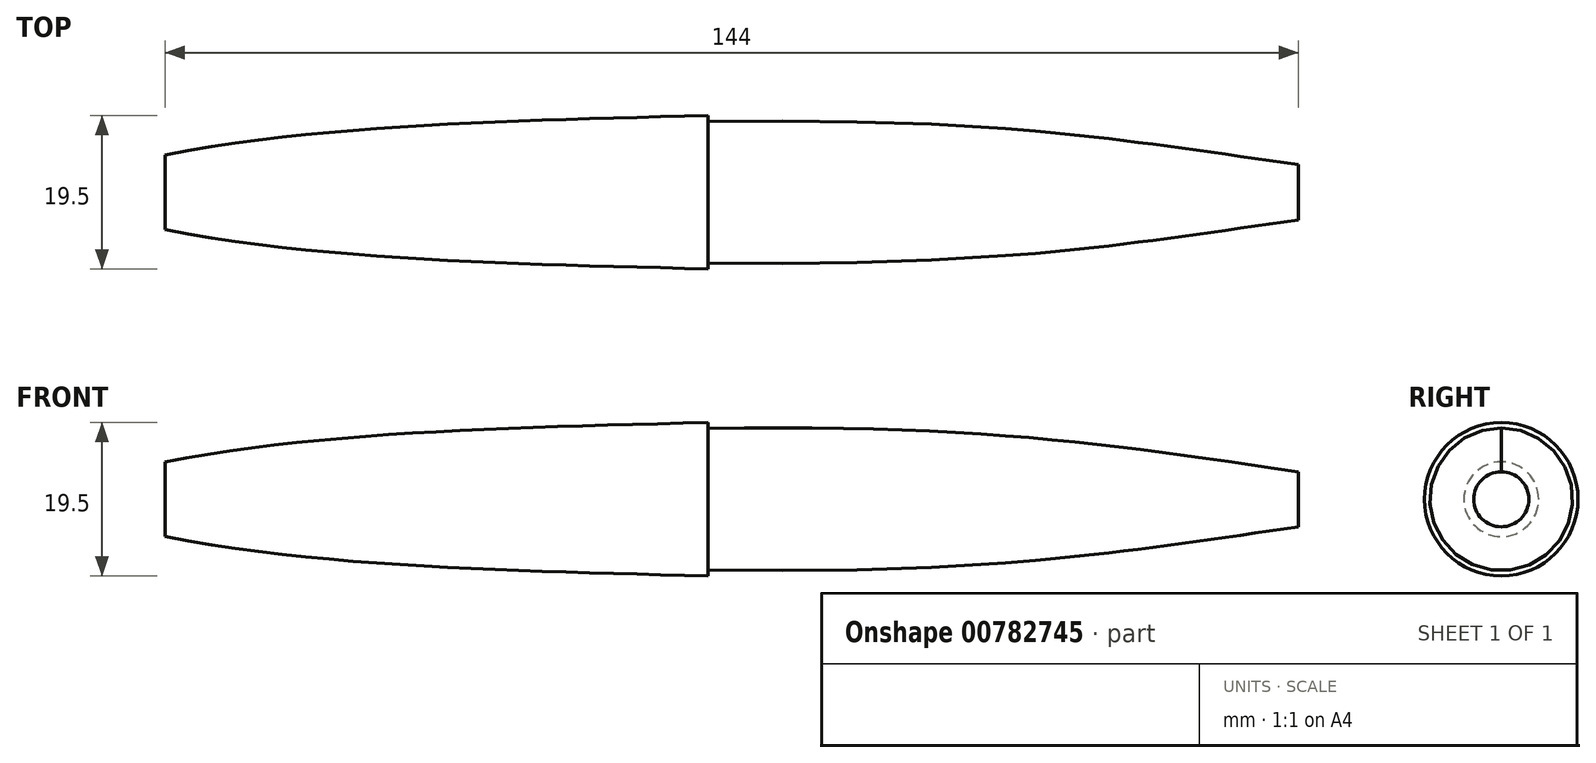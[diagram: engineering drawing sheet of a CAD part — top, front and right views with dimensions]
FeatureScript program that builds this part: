
annotation { "Feature Type Name" : "Feature", "Feature Type Description" : "" }
export const myFeature = defineFeature(function(context is Context, id is Id, definition is map)
    precondition{}
    {
        {
            var Q0;
            Q0=qCreatedBy(makeId("Front.planeOp"),FACE);
            var sketch = newSketch(context, id + "F0", { "sketchPlane" : qUnion([Q0])});
            skLineSegment(sketch, "E0", {"start": v(75, 3.5) * mm, "end": v(75, 0) * mm});
            skLineSegment(sketch, "E1", {"start": v(0, 9) * mm, "end": v(0, 0) * mm});
            skLineSegment(sketch, "E2", {"start": v(0, 9.75) * mm, "end": v(0, 0) * mm});
            skLineSegment(sketch, "E3", {"start": v(-69, 4.75) * mm, "end": v(-69, 0) * mm});
            skFitSpline(sketch, "E4", {"points": [v(0, 9) * mm, v(75, 3.5) * mm], "startDerivative": vector(109.15, 1.42) * mm, "endDerivative": vector(71.22, -10.16) * mm});
            skFitSpline(sketch, "E5", {"points": [v(-69, 4.75) * mm, v(0, 9.75) * mm], "startDerivative": vector(61.77, 11.96) * mm, "endDerivative": vector(74.26, 2.03) * mm});
            skLineSegment(sketch, "E6", {"start": v(-69, 0) * mm, "end": v(75, 0) * mm});
            skSolve(sketch);
        }
        {
            var Q0;
            Q0 = qSketchRegion(id + "F0", true);
            var Q1;
            Q1=sQuery(id+"F0.wireOp",EDGE,"E6");
            revolve(context, id + "F1", {"surfaceOperationType" : NewSurfaceOperationType.NEW, "entities" : qUnion([Q0]), "axis" : qUnion([Q1]), "revolveType" : RevolveType.FULL});
        }
    });
